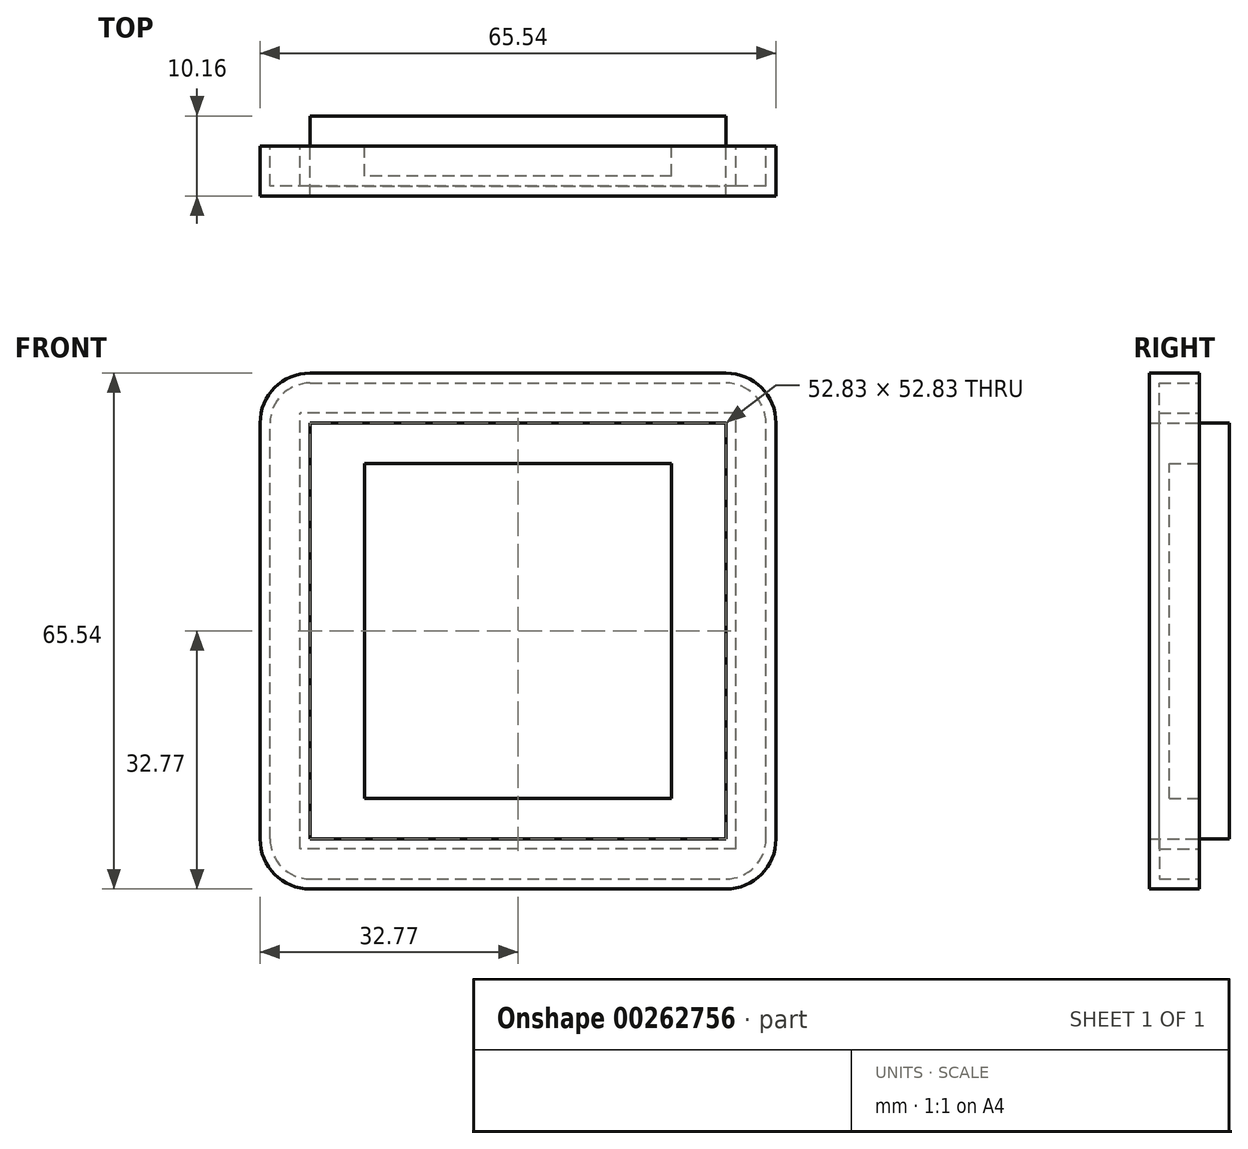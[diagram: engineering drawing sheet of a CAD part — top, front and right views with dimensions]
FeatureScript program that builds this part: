
annotation { "Feature Type Name" : "Feature", "Feature Type Description" : "" }
export const myFeature = defineFeature(function(context is Context, id is Id, definition is map)
    precondition{}
    {
        {
            var Q0;
            Q0=qCreatedBy(makeId("Front.planeOp"),FACE);
            var sketch = newSketch(context, id + "F0", { "sketchPlane" : qUnion([Q0])});
            skLineSegment(sketch, "E0.bottom", {"start": v(-26.42, -32.77) * mm, "end": v(26.42, -32.77) * mm});
            skLineSegment(sketch, "E0.top", {"start": v(-26.42, 32.77) * mm, "end": v(26.42, 32.77) * mm});
            skLineSegment(sketch, "E0.left", {"start": v(-32.77, -26.42) * mm, "end": v(-32.77, 26.42) * mm});
            skLineSegment(sketch, "E0.right", {"start": v(32.77, -26.42) * mm, "end": v(32.77, 26.42) * mm});
            skPoint(sketch, "E0.middle", {"position": v(0, 0) * mm});
            skPoint(sketch, "E1.visualSharp", {"position": v(-32.77, 32.77) * mm});
            skArc(sketch, "E1.filletArc", {"start": v(-26.42, 32.77) * mm, "mid": v(-30.9, 30.9) * mm, "end": v(-32.77, 26.42) * mm});
            skPoint(sketch, "E2.visualSharp", {"position": v(32.77, 32.77) * mm});
            skArc(sketch, "E2.filletArc", {"start": v(32.77, 26.42) * mm, "mid": v(30.9, 30.9) * mm, "end": v(26.42, 32.77) * mm});
            skPoint(sketch, "E3.visualSharp", {"position": v(32.77, -32.77) * mm});
            skArc(sketch, "E3.filletArc", {"start": v(26.42, -32.77) * mm, "mid": v(30.9, -30.9) * mm, "end": v(32.77, -26.42) * mm});
            skPoint(sketch, "E4.visualSharp", {"position": v(-32.77, -32.77) * mm});
            skArc(sketch, "E4.filletArc", {"start": v(-32.77, -26.42) * mm, "mid": v(-30.9, -30.9) * mm, "end": v(-26.42, -32.77) * mm});
            skLineSegment(sketch, "E5.bottom", {"start": v(26.42, -26.42) * mm, "end": v(-26.42, -26.42) * mm});
            skLineSegment(sketch, "E5.top", {"start": v(26.42, 26.42) * mm, "end": v(-26.42, 26.42) * mm});
            skLineSegment(sketch, "E5.left", {"start": v(26.42, -26.42) * mm, "end": v(26.42, 26.42) * mm});
            skLineSegment(sketch, "E5.right", {"start": v(-26.42, -26.42) * mm, "end": v(-26.42, 26.42) * mm});
            skLineSegment(sketch, "E6.bottom", {"start": v(19.5, -21.28) * mm, "end": v(-19.5, -21.28) * mm});
            skLineSegment(sketch, "E6.top", {"start": v(19.5, 21.28) * mm, "end": v(-19.5, 21.28) * mm});
            skLineSegment(sketch, "E6.left", {"start": v(19.5, -21.28) * mm, "end": v(19.5, 21.28) * mm});
            skLineSegment(sketch, "E6.right", {"start": v(-19.5, -21.28) * mm, "end": v(-19.5, 21.28) * mm});
            skSolve(sketch);
        }
        {
            var Q0;
            Q0 = qSketchRegion(id + "F0", true);
            extrude(context, id + "F1", {"entities" : qUnion([Q0]), "depth" : 6.35 * mm});
        }
        {
            var Q0;
            Q0=makeQuery(id+"F0.imprint","IMPRINT",FACE,{"disambiguationData":[TD([[makeQuery(id+"F0.imprint","IMPRINT",EDGE,{"derivedFrom":sQuery(id+"F0.wireOp",EDGE,"E5.bottom")}),-1.0]])]});
            var Q1;
            Q1=makeQuery(id+"F0.imprint","IMPRINT",FACE,{"disambiguationData":[TD([[makeQuery(id+"F0.imprint","IMPRINT",EDGE,{"derivedFrom":sQuery(id+"F0.wireOp",EDGE,"E6.bottom")}),-1.0]])]});
            extrude(context, id + "F2", {"entities" : qUnion([Q0, Q1]), "oppositeDirection" : true, "depth" : 3.8 * mm});
        }
        {
            var Q0;
            Q0=makeQuery(id+"F0.imprint","IMPRINT",FACE,{"disambiguationData":[TD([[makeQuery(id+"F0.imprint","IMPRINT",EDGE,{"derivedFrom":sQuery(id+"F0.wireOp",EDGE,"E6.bottom")}),-1.0]])]});
            extrude(context, id + "F3", {"entities" : qUnion([Q0]), "operationType" : NewBodyOperationType.ADD, "depth" : 3.8 * mm});
        }
        {
            var Q0;
            Q0=makeQuery(id+"F1.opExtrude","CAP_FACE",FACE,{"disambiguationData":[OSD([sQuery(id+"F0.wireOp",EDGE,"E0.bottom"),sQuery(id+"F0.wireOp",EDGE,"E0.top"),sQuery(id+"F0.wireOp",EDGE,"E0.left"),sQuery(id+"F0.wireOp",EDGE,"E0.right"),sQuery(id+"F0.wireOp",EDGE,"E1.filletArc"),sQuery(id+"F0.wireOp",EDGE,"E2.filletArc"),sQuery(id+"F0.wireOp",EDGE,"E3.filletArc"),sQuery(id+"F0.wireOp",EDGE,"E4.filletArc"),sQuery(id+"F0.wireOp",EDGE,"E5.bottom"),sQuery(id+"F0.wireOp",EDGE,"E5.top"),sQuery(id+"F0.wireOp",EDGE,"E5.left"),sQuery(id+"F0.wireOp",EDGE,"E5.right")])],"isStart":true});
            shell(context, id + "F4", {"entities" : qUnion([Q0]), "thickness" : 1.27 * mm});
        }
    });
